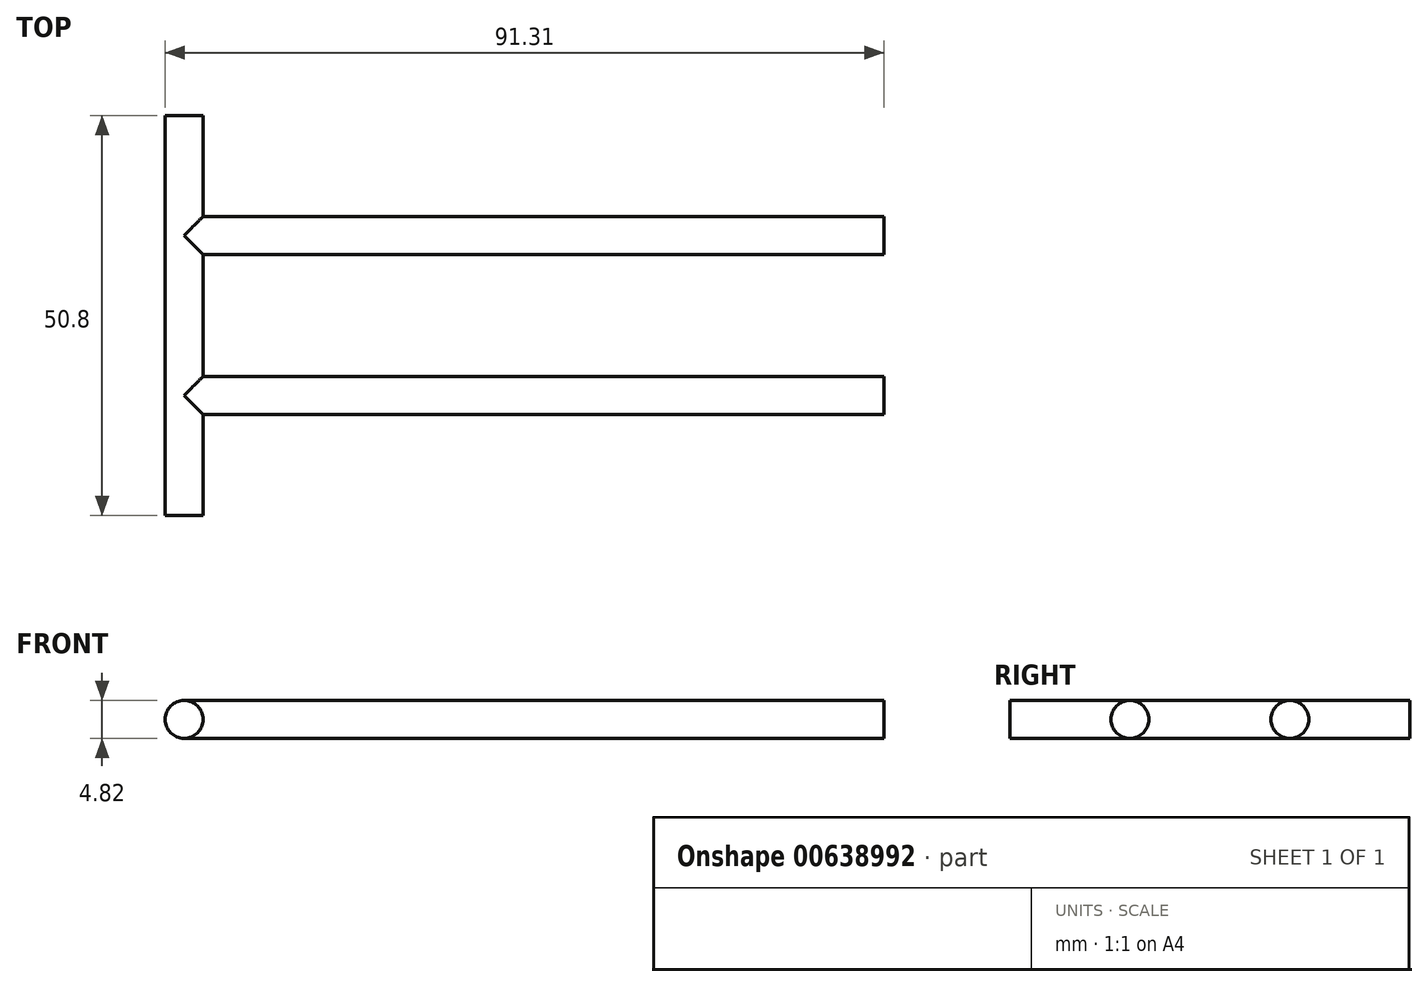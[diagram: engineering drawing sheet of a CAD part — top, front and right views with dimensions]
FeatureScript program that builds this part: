
annotation { "Feature Type Name" : "Feature", "Feature Type Description" : "" }
export const myFeature = defineFeature(function(context is Context, id is Id, definition is map)
    precondition{}
    {
        {
            var Q0;
            Q0=qCreatedBy(makeId("Front.planeOp"),FACE);
            var sketch = newSketch(context, id + "F0", { "sketchPlane" : qUnion([Q0])});
            skCircle(sketch, "E0", {"center": v(0, 0) * mm, "radius": 2.41 * mm});
            skSolve(sketch);
        }
        {
            var Q0;
            Q0=makeQuery(id+"F0.imprint","IMPRINT",FACE,{"disambiguationData":[TD([[makeQuery(id+"F0.imprint","IMPRINT",EDGE,{"derivedFrom":sQuery(id+"F0.wireOp",EDGE,"E0")}),1.0]])]});
            extrude(context, id + "F1", {"entities" : qUnion([Q0]), "depth" : 50.8 * mm});
        }
        {
            var Q0;
            Q0=qCreatedBy(makeId("Right.planeOp"),FACE);
            var sketch = newSketch(context, id + "F2", { "sketchPlane" : qUnion([Q0])});
            skPoint(sketch, "E1", {"position": v(0, 0) * mm});
            skPoint(sketch, "E2", {"position": v(-35.56, 2.41) * mm});
            skPoint(sketch, "E3", {"position": v(-15.24, 2.41) * mm});
            skPoint(sketch, "E4", {"position": v(-15.24, 0) * mm});
            skPoint(sketch, "E5", {"position": v(-35.56, 0) * mm});
            skCircle(sketch, "E6", {"center": v(-35.56, 0) * mm, "radius": 2.41 * mm});
            skCircle(sketch, "E7", {"center": v(-15.24, 0) * mm, "radius": 2.41 * mm});
            skSolve(sketch);
        }
        {
            var Q0;
            Q0=qSketchRegion(id+"F2",true);
            extrude(context, id + "F3", {"entities" : qUnion([Q0]), "operationType" : NewBodyOperationType.ADD, "depth" : 88.9 * mm});
        }
    });
